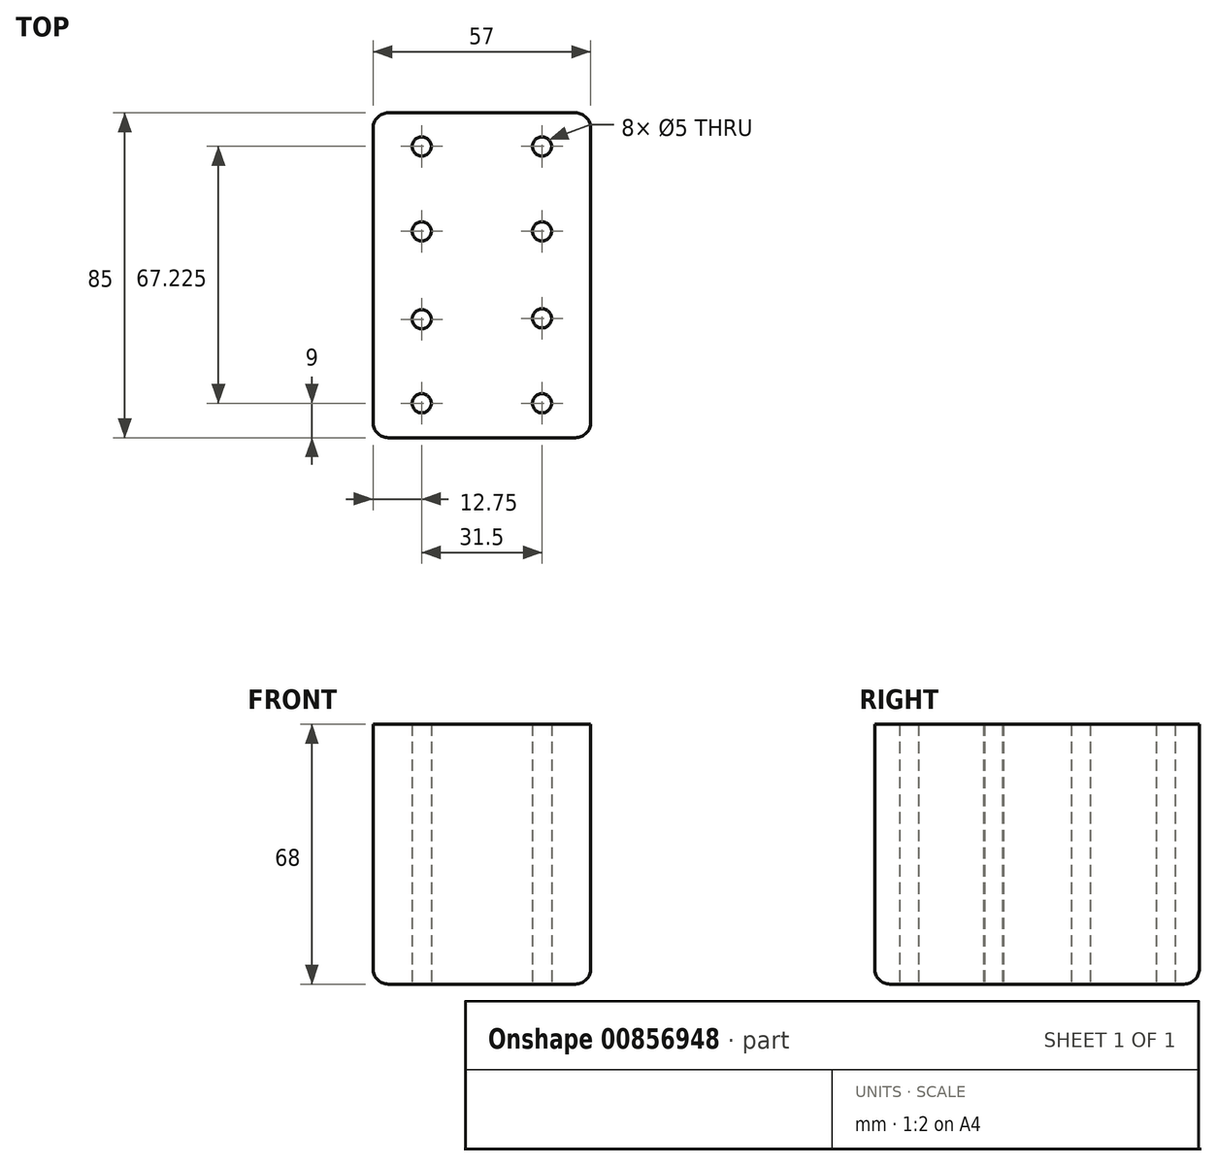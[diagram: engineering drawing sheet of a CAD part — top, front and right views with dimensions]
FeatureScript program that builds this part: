
annotation { "Feature Type Name" : "Feature", "Feature Type Description" : "" }
export const myFeature = defineFeature(function(context is Context, id is Id, definition is map)
    precondition{}
    {
        {
            var Q0;
            Q0=qCreatedBy(makeId("Top.planeOp"),FACE);
            var sketch = newSketch(context, id + "F0", { "sketchPlane" : qUnion([Q0])});
            skLineSegment(sketch, "E0.bottom", {"start": v(0, 0) * mm, "end": v(-57, 0) * mm});
            skLineSegment(sketch, "E0.top", {"start": v(0, 63) * mm, "end": v(-57, 63) * mm});
            skLineSegment(sketch, "E0.left", {"start": v(0, 0) * mm, "end": v(0, 63) * mm});
            skLineSegment(sketch, "E0.right", {"start": v(-57, 0) * mm, "end": v(-57, 63) * mm});
            skLineSegment(sketch, "E1", {"start": v(-4, 54.22) * mm, "end": v(-53, 54.22) * mm});
            skLineSegment(sketch, "E2", {"start": v(-28.5, 54.22) * mm, "end": v(-12.75, 54.22) * mm});
            skCircle(sketch, "E3", {"center": v(-12.75, 54.22) * mm, "radius": 2.5 * mm});
            skLineSegment(sketch, "E4", {"start": v(-28.5, 54.22) * mm, "end": v(-28.5, 31.72) * mm});
            skLineSegment(sketch, "E5", {"start": v(-30.3, 31.72) * mm, "end": v(-28.5, 31.72) * mm});
            skCircle(sketch, "E6.MirrorC", {"center": v(-12.75, 9.22) * mm, "radius": 2.5 * mm});
            skCircle(sketch, "E7.MirrorC", {"center": v(-44.25, 9) * mm, "radius": 2.5 * mm});
            skLineSegment(sketch, "E8", {"start": v(-44.25, 9) * mm, "end": v(-57, 9) * mm});
            skLineSegment(sketch, "E9", {"start": v(-44.25, 9) * mm, "end": v(-44.25, 0) * mm});
            skCircle(sketch, "E10", {"center": v(-44.25, 54.22) * mm, "radius": 2.5 * mm});
            skLineSegment(sketch, "E11", {"start": v(-57, 0) * mm, "end": v(-57, -22) * mm});
            skLineSegment(sketch, "E12", {"start": v(-57, -22) * mm, "end": v(0, -22) * mm});
            skLineSegment(sketch, "E13", {"start": v(0, -22) * mm, "end": v(0, 0) * mm});
            skLineSegment(sketch, "E14", {"start": v(-44.25, 0) * mm, "end": v(-44.25, -13) * mm});
            skLineSegment(sketch, "E15", {"start": v(-44.25, -13) * mm, "end": v(-12.75, -13) * mm});
            skCircle(sketch, "E16", {"center": v(-44.25, -13) * mm, "radius": 2.5 * mm});
            skCircle(sketch, "E17", {"center": v(-12.75, -13) * mm, "radius": 2.5 * mm});
            skLineSegment(sketch, "E18", {"start": v(-28.5, -13) * mm, "end": v(-28.5, 9.5) * mm});
            skLineSegment(sketch, "E19", {"start": v(-28.5, 9.5) * mm, "end": v(-24.48, 9.5) * mm});
            skCircle(sketch, "E20.MirrorC", {"center": v(-12.75, 32) * mm, "radius": 2.5 * mm});
            skCircle(sketch, "E21.MirrorC", {"center": v(-44.25, 32) * mm, "radius": 2.5 * mm});
            skSolve(sketch);
        }
        {
            var Q0;
            Q0=qSketchRegion(id+"F0",true);
            var Q1;
            {var subQ3=sQuery(id+"F0.wireOp",EDGE,"E15");var subQ5=sQuery(id+"F0.wireOp",EDGE,"E18");var subQ6=makeQuery(id+"F0.imprint","INTERSECT",VERTEX,{"derivedFrom":[subQ3,subQ5]});Q1=makeQuery(id+"F0.imprint","IMPRINT",FACE,{"disambiguationData":[TD([[makeQuery(id+"F0.imprint","IMPRINT",EDGE,{"disambiguationData":[TD([[subQ6,1.0]])],"derivedFrom":subQ3}),1.0]])]});}
            extrude(context, id + "F1", {"entities" : qUnion([Q0, Q1]), "offsetDistance" : 25 * mm, "depth" : 68 * mm});
        }
        {
            var Q0;
            Q0=makeQuery(id+"F1.opExtrude","CAP_EDGE",EDGE,{"disambiguationData":[OSD([sQuery(id+"F0.wireOp",EDGE,"E0.top")])],"isStart":true});
            var Q1;
            Q1=makeQuery(id+"F1.opExtrude","CAP_EDGE",EDGE,{"disambiguationData":[OSD([sQuery(id+"F0.wireOp",EDGE,"E0.left")])],"isStart":true});
            var Q2;
            Q2=makeQuery(id+"F1.opExtrude","CAP_EDGE",EDGE,{"disambiguationData":[OSD([sQuery(id+"F0.wireOp",EDGE,"E0.bottom")])],"isStart":true});
            var Q3;
            Q3=makeQuery(id+"F1.opExtrude","CAP_EDGE",EDGE,{"disambiguationData":[OSD([sQuery(id+"F0.wireOp",EDGE,"E0.right")])],"isStart":true});
            var Q4;
            Q4=makeQuery(id+"F1.opExtrude","SWEPT_EDGE",EDGE,{"disambiguationData":[OSD([sQuery(id+"F0.wireOp",EDGE,"E0.bottom"),sQuery(id+"F0.wireOp",EDGE,"E0.right")])]});
            var Q5;
            Q5=makeQuery(id+"F1.opExtrude","SWEPT_EDGE",EDGE,{"disambiguationData":[OSD([sQuery(id+"F0.wireOp",EDGE,"E0.top"),sQuery(id+"F0.wireOp",EDGE,"E0.right")])]});
            var Q6;
            Q6=makeQuery(id+"F1.opExtrude","SWEPT_EDGE",EDGE,{"disambiguationData":[OSD([sQuery(id+"F0.wireOp",EDGE,"E0.top"),sQuery(id+"F0.wireOp",EDGE,"E0.left")])]});
            var Q7;
            Q7=makeQuery(id+"F1.opExtrude","SWEPT_EDGE",EDGE,{"disambiguationData":[OSD([sQuery(id+"F0.wireOp",EDGE,"E0.bottom"),sQuery(id+"F0.wireOp",EDGE,"E0.left")])]});
            var Q8;
            Q8=makeQuery(id+"F1.opExtrude","CAP_EDGE",EDGE,{"disambiguationData":[OSD([sQuery(id+"F0.wireOp",EDGE,"E12")])],"isStart":true});
            var Q9;
            Q9=makeQuery(id+"F1.opExtrude","SWEPT_EDGE",EDGE,{"disambiguationData":[OSD([sQuery(id+"F0.wireOp",EDGE,"E11"),sQuery(id+"F0.wireOp",EDGE,"E12")])]});
            var Q10;
            Q10=makeQuery(id+"F1.opExtrude","SWEPT_EDGE",EDGE,{"disambiguationData":[OSD([sQuery(id+"F0.wireOp",EDGE,"E12"),sQuery(id+"F0.wireOp",EDGE,"E13")])]});
            fillet(context, id + "F2", {"entities" : qUnion([Q0, Q1, Q2, Q3, Q4, Q5, Q6, Q7, Q8, Q9, Q10]), "radius" : 4 * mm, "tangentPropagation" : true, "allowEdgeOverflow" : false});
        }
    });
